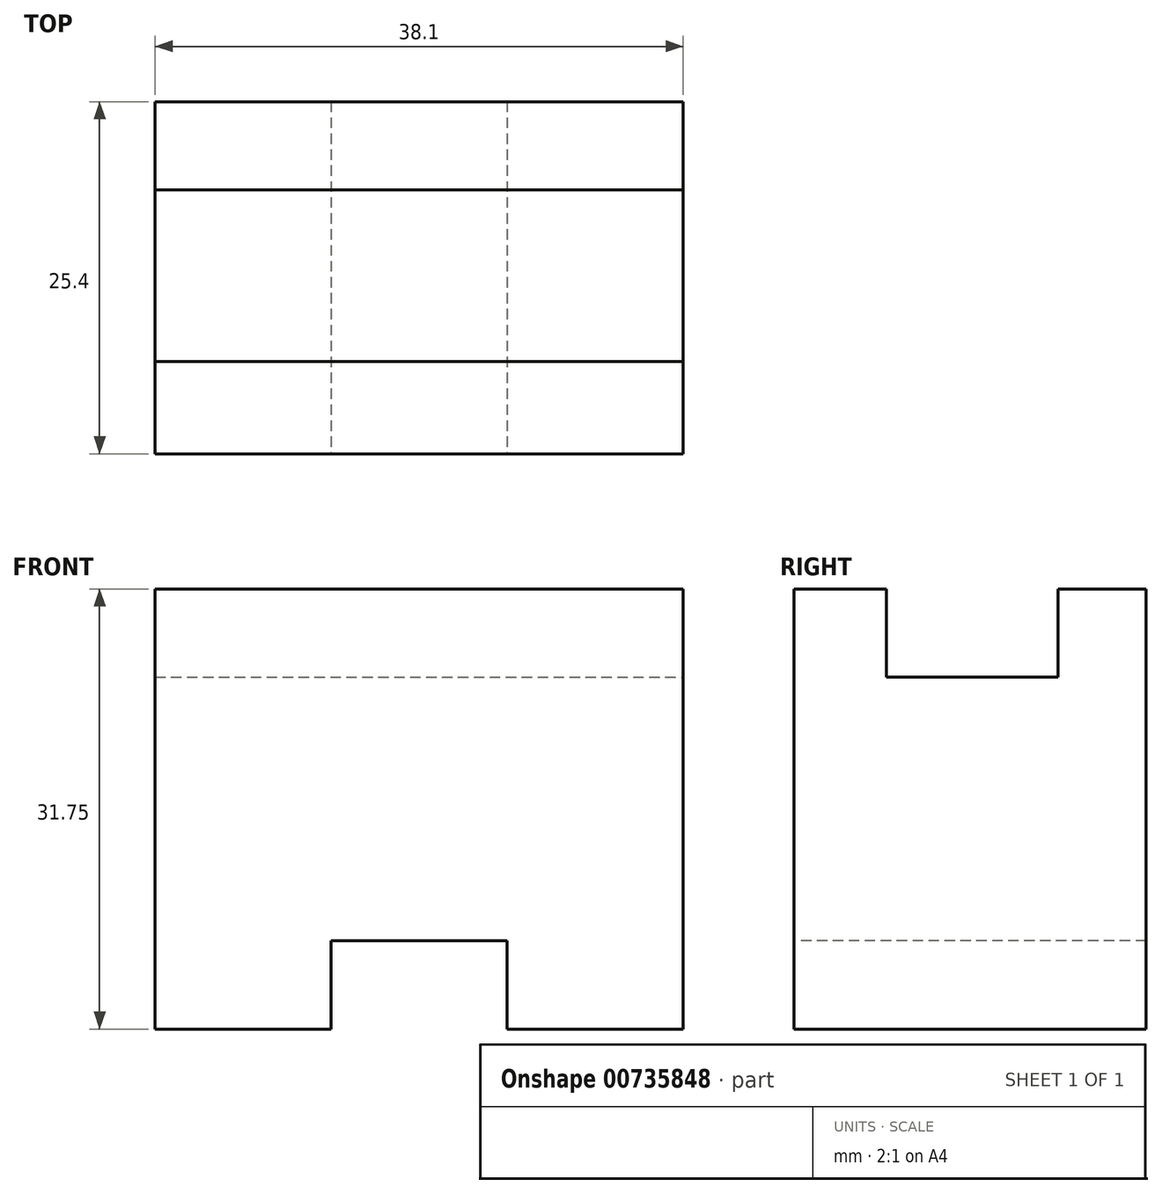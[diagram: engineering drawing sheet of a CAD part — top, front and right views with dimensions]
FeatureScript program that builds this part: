
annotation { "Feature Type Name" : "Feature", "Feature Type Description" : "" }
export const myFeature = defineFeature(function(context is Context, id is Id, definition is map)
    precondition{}
    {
        {
            var Q0;
            Q0=qCreatedBy(makeId("Right.planeOp"),FACE);
            var sketch = newSketch(context, id + "F0", { "sketchPlane" : qUnion([Q0])});
            skLineSegment(sketch, "E0", {"start": v(0, 0) * mm, "end": v(25.4, 0) * mm});
            skLineSegment(sketch, "E1", {"start": v(25.4, 0) * mm, "end": v(25.4, 31.75) * mm});
            skLineSegment(sketch, "E2", {"start": v(25.4, 31.75) * mm, "end": v(0, 31.75) * mm});
            skLineSegment(sketch, "E3", {"start": v(0, 31.75) * mm, "end": v(0, 0) * mm});
            skSolve(sketch);
        }
        {
            var Q0;
            Q0 = qSketchRegion(id + "F0", true);
            extrude(context, id + "F1", {"entities" : qUnion([Q0]), "depth" : 38.1 * mm, "offsetDistance" : 25.4 * mm});
        }
        {
            var Q0;
            Q0=makeQuery(id+"F1.opExtrude","CAP_FACE",FACE,{"disambiguationData":[OSD([sQuery(id+"F0.wireOp",EDGE,"E0"),sQuery(id+"F0.wireOp",EDGE,"E1"),sQuery(id+"F0.wireOp",EDGE,"E2"),sQuery(id+"F0.wireOp",EDGE,"E3")])],"isStart":false});
            var sketch = newSketch(context, id + "F2", { "sketchPlane" : qUnion([Q0])});
            skLineSegment(sketch, "E4", {"start": v(12.7, 31.75) * mm, "end": v(12.7, 25.4) * mm});
            skLineSegment(sketch, "E5", {"start": v(12.7, 25.4) * mm, "end": v(19.05, 25.4) * mm});
            skLineSegment(sketch, "E6", {"start": v(19.05, 25.4) * mm, "end": v(19.05, 31.75) * mm});
            skLineSegment(sketch, "E7", {"start": v(19.05, 31.75) * mm, "end": v(12.7, 31.75) * mm});
            skSolve(sketch);
        }
        {
            var Q0;
            Q0=makeQuery(id+"F2.imprint","IMPRINT",FACE,{"disambiguationData":[TD([[makeQuery(id+"F2.imprint","IMPRINT",EDGE,{"derivedFrom":sQuery(id+"F2.wireOp",EDGE,"E4")}),1.0]])]});
            extrude(context, id + "F3", {"entities" : qUnion([Q0]), "operationType" : NewBodyOperationType.REMOVE, "oppositeDirection" : true, "depth" : 38.1 * mm, "offsetDistance" : 25.4 * mm});
        }
        {
            var Q0;
            Q0=makeQuery(id+"F1.opExtrude","CAP_FACE",FACE,{"disambiguationData":[OSD([sQuery(id+"F0.wireOp",EDGE,"E0"),sQuery(id+"F0.wireOp",EDGE,"E1"),sQuery(id+"F0.wireOp",EDGE,"E2"),sQuery(id+"F0.wireOp",EDGE,"E3")])],"isStart":false});
            var sketch = newSketch(context, id + "F4", { "sketchPlane" : qUnion([Q0])});
            skLineSegment(sketch, "E8", {"start": v(12.7, 25.4) * mm, "end": v(6.67, 25.4) * mm});
            skLineSegment(sketch, "E9", {"start": v(6.67, 25.4) * mm, "end": v(6.67, 31.75) * mm});
            skLineSegment(sketch, "E10", {"start": v(6.67, 31.75) * mm, "end": v(12.7, 31.75) * mm});
            skLineSegment(sketch, "E11", {"start": v(12.7, 31.75) * mm, "end": v(12.7, 25.4) * mm});
            skSolve(sketch);
        }
        {
            var Q0;
            Q0=makeQuery(id+"F4.imprint","IMPRINT",FACE,{"disambiguationData":[TD([[makeQuery(id+"F4.imprint","IMPRINT",EDGE,{"derivedFrom":sQuery(id+"F4.wireOp",EDGE,"E8")}),-1.0]])]});
            extrude(context, id + "F5", {"entities" : qUnion([Q0]), "operationType" : NewBodyOperationType.REMOVE, "oppositeDirection" : true, "depth" : 38.1 * mm, "offsetDistance" : 25.4 * mm});
        }
        {
            var Q0;
            Q0=makeQuery(id+"F1.opExtrude","SWEPT_FACE",FACE,{"disambiguationData":[OSD([sQuery(id+"F0.wireOp",EDGE,"E3")])]});
            var sketch = newSketch(context, id + "F6", { "sketchPlane" : qUnion([Q0])});
            skLineSegment(sketch, "E12", {"start": v(19.05, 0) * mm, "end": v(19.05, 6.36) * mm});
            skLineSegment(sketch, "E13", {"start": v(19.05, 6.36) * mm, "end": v(12.7, 6.36) * mm});
            skLineSegment(sketch, "E14", {"start": v(12.7, 6.36) * mm, "end": v(12.7, 0) * mm});
            skLineSegment(sketch, "E15", {"start": v(12.7, 0) * mm, "end": v(19.05, 0) * mm});
            skSolve(sketch);
        }
        {
            var Q0;
            Q0=makeQuery(id+"F6.imprint","IMPRINT",FACE,{"disambiguationData":[TD([[makeQuery(id+"F6.imprint","IMPRINT",EDGE,{"derivedFrom":sQuery(id+"F6.wireOp",EDGE,"E12")}),1.0]])]});
            extrude(context, id + "F7", {"entities" : qUnion([Q0]), "operationType" : NewBodyOperationType.REMOVE, "oppositeDirection" : true, "depth" : 38.1 * mm, "offsetDistance" : 25.4 * mm});
        }
        {
            var Q0;
            Q0=makeQuery(id+"F1.opExtrude","SWEPT_FACE",FACE,{"disambiguationData":[OSD([sQuery(id+"F0.wireOp",EDGE,"E3")])]});
            var sketch = newSketch(context, id + "F8", { "sketchPlane" : qUnion([Q0])});
            skLineSegment(sketch, "E16", {"start": v(19.05, 6.36) * mm, "end": v(25.4, 6.36) * mm});
            skLineSegment(sketch, "E17", {"start": v(25.4, 6.36) * mm, "end": v(25.4, 0) * mm});
            skLineSegment(sketch, "E18", {"start": v(25.4, 0) * mm, "end": v(19.05, 0) * mm});
            skLineSegment(sketch, "E19", {"start": v(19.05, 0) * mm, "end": v(19.05, 6.36) * mm});
            skSolve(sketch);
        }
        {
            var Q0;
            Q0=makeQuery(id+"F8.imprint","IMPRINT",FACE,{"disambiguationData":[TD([[makeQuery(id+"F8.imprint","IMPRINT",EDGE,{"derivedFrom":sQuery(id+"F8.wireOp",EDGE,"E16")}),-1.0]])]});
            extrude(context, id + "F9", {"entities" : qUnion([Q0]), "operationType" : NewBodyOperationType.REMOVE, "oppositeDirection" : true, "depth" : 38.1 * mm, "offsetDistance" : 25.4 * mm});
        }
    });
